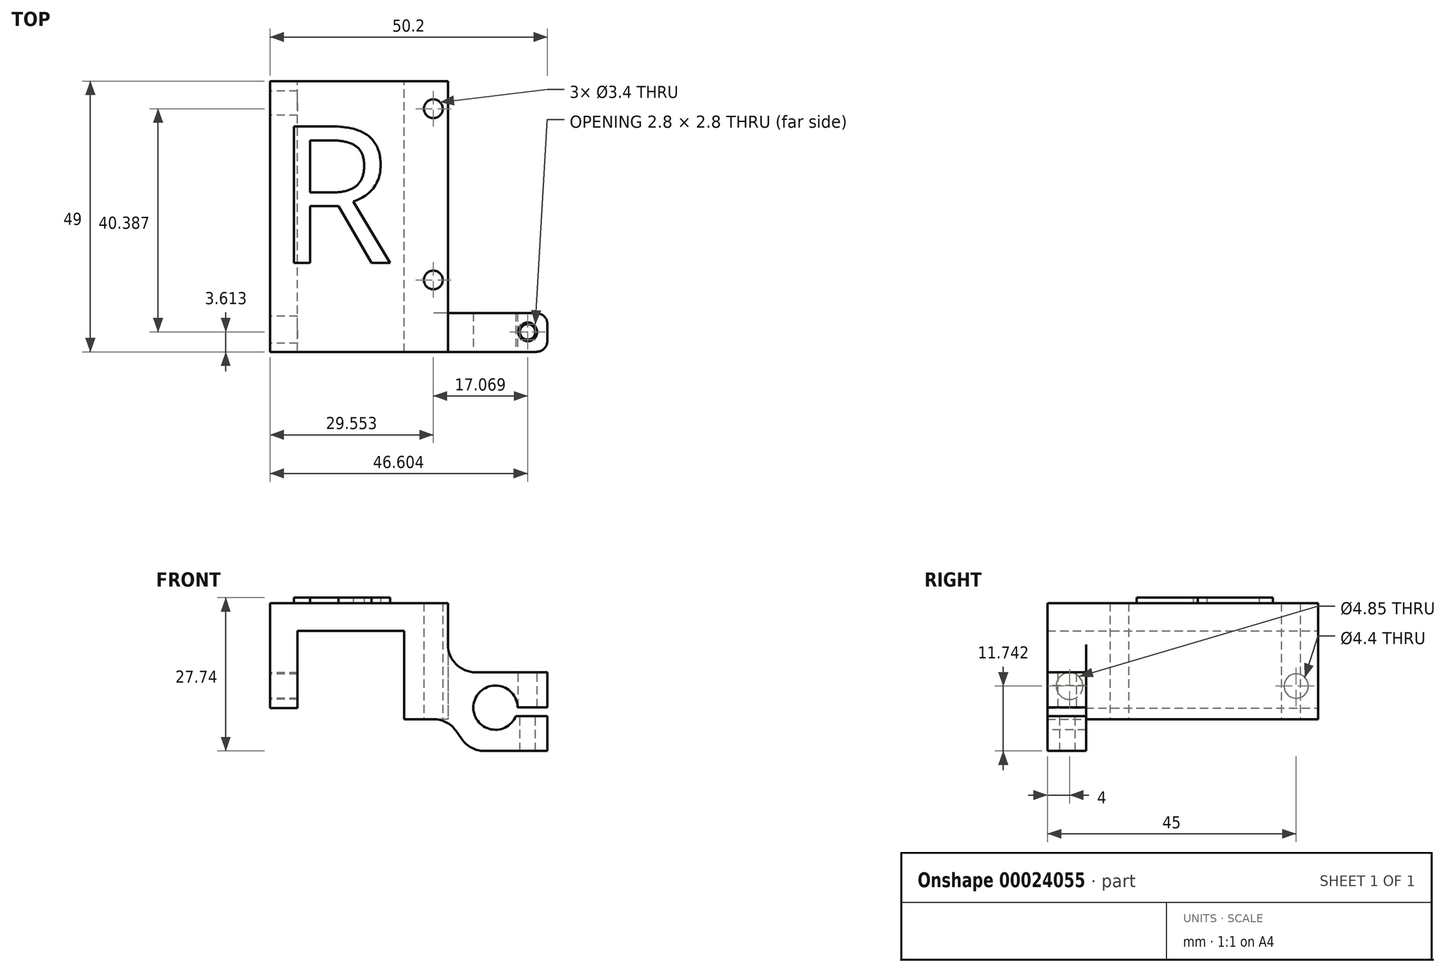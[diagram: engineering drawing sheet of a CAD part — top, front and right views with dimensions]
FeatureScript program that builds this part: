
annotation { "Feature Type Name" : "Feature", "Feature Type Description" : "" }
export const myFeature = defineFeature(function(context is Context, id is Id, definition is map)
    precondition{}
    {
        {
            var Q0;
            Q0=qCreatedBy(makeId("Front.planeOp"),FACE);
            var sketch = newSketch(context, id + "F0", { "sketchPlane" : qUnion([Q0])});
            skLineSegment(sketch, "E0", {"start": v(-18.67, 10.9) * mm, "end": v(-18.67, 29.9) * mm});
            skLineSegment(sketch, "E1", {"start": v(-18.67, 29.9) * mm, "end": v(13.53, 29.9) * mm});
            skLineSegment(sketch, "E2", {"start": v(13.53, 29.9) * mm, "end": v(13.53, 17.4) * mm});
            skLineSegment(sketch, "E3", {"start": v(5.63, 8.9) * mm, "end": v(5.63, 24.9) * mm});
            skLineSegment(sketch, "E4", {"start": v(5.63, 24.9) * mm, "end": v(-13.67, 24.9) * mm});
            skLineSegment(sketch, "E5", {"start": v(-13.67, 24.9) * mm, "end": v(-13.67, 10.9) * mm});
            skLineSegment(sketch, "E6", {"start": v(-13.67, 10.9) * mm, "end": v(-18.67, 10.9) * mm});
            skLineSegment(sketch, "E7", {"start": v(13.53, 17.4) * mm, "end": v(13.53, 8.9) * mm});
            skLineSegment(sketch, "E8", {"start": v(13.53, 8.9) * mm, "end": v(5.63, 8.9) * mm});
            skLineSegment(sketch, "E9", {"start": v(13.53, 17.4) * mm, "end": v(13.53, 17.4) * mm});
            skLineSegment(sketch, "E10", {"start": v(31.53, 17.36) * mm, "end": v(31.53, 11.06) * mm});
            skLineSegment(sketch, "E11", {"start": v(31.53, 11.06) * mm, "end": v(24.33, 11.06) * mm});
            skLineSegment(sketch, "E12", {"start": v(24.33, 11.06) * mm, "end": v(24.33, 9.45) * mm});
            skLineSegment(sketch, "E13", {"start": v(24.33, 9.45) * mm, "end": v(31.53, 9.45) * mm});
            skLineSegment(sketch, "E14", {"start": v(31.53, 9.45) * mm, "end": v(31.53, 3.15) * mm});
            skLineSegment(sketch, "E15", {"start": v(31.53, 3.15) * mm, "end": v(17.53, 3.15) * mm});
            skLineSegment(sketch, "E16", {"start": v(17.53, 3.15) * mm, "end": v(13.53, 8.9) * mm});
            skLineSegment(sketch, "E17", {"start": v(31.53, 17.36) * mm, "end": v(13.53, 17.4) * mm});
            skSolve(sketch);
        }
        {
            var Q0;
            Q0=makeQuery(id+"F0.imprint","IMPRINT",FACE,{"disambiguationData":[TD([[makeQuery(id+"F0.imprint","IMPRINT",EDGE,{"derivedFrom":sQuery(id+"F0.wireOp",EDGE,"E0")}),-1.0]])]});
            var Q1;
            {var subQ2=sQuery(id+"F0.wireOp",EDGE,"69cbcc5d-e0c3-48db-8baf-3487a8abab7d");Q1=makeQuery(id+"F0.imprint","IMPRINT",FACE,{"disambiguationData":[TD([[makeQuery(id+"F0.imprint","IMPRINT",EDGE,{"derivedFrom":subQ2}),-1.0]])]});}
            var Q2;
            Q2=makeQuery(id+"F0.imprint","IMPRINT",FACE,{"disambiguationData":[TD([[makeQuery(id+"F0.imprint","IMPRINT",EDGE,{"derivedFrom":sQuery(id+"F0.wireOp",EDGE,"E7")}),1.0]])]});
            extrude(context, id + "F1", {"entities" : qUnion([Q0, Q1, Q2]), "depth" : 7 * mm});
        }
        {
            var Q0;
            Q0=makeQuery(id+"F0.imprint","IMPRINT",FACE,{"disambiguationData":[TD([[makeQuery(id+"F0.imprint","IMPRINT",EDGE,{"derivedFrom":sQuery(id+"F0.wireOp",EDGE,"E0")}),-1.0]])]});
            extrude(context, id + "F2", {"entities" : qUnion([Q0]), "operationType" : NewBodyOperationType.ADD, "oppositeDirection" : true, "depth" : 42 * mm});
        }
        {
            var Q0;
            {var subQ0=sQuery(id+"F0.wireOp",EDGE,"E8");Q0=makeQuery(id+"F2.boolean.opBoolean","MERGE",FACE,{"derivedFrom":[makeQuery(id+"F1.opExtrude","SWEPT_FACE",FACE,{"disambiguationData":[OSD([subQ0])]}),makeQuery(id+"F2.opExtrude","SWEPT_FACE",FACE,{"disambiguationData":[OSD([subQ0])]})]});}
            var sketch = newSketch(context, id + "F3", { "sketchPlane" : qUnion([Q0])});
            skCircle(sketch, "E18", {"center": v(10.88, -6) * mm, "radius": 1.7 * mm});
            skCircle(sketch, "E19", {"center": v(10.88, -37) * mm, "radius": 1.7 * mm});
            skCircle(sketch, "E20", {"center": v(26.38, -21.5) * mm, "radius": 11 * mm});
            skSolve(sketch);
        }
        {
            var Q0;
            Q0=qSketchRegion(id+"F3",true);
            extrude(context, id + "F4", {"entities" : qUnion([Q0]), "operationType" : NewBodyOperationType.REMOVE, "endBound" : BoundingType.THROUGH_ALL, "oppositeDirection" : true, "depth" : 25 * mm});
        }
        {
            var Q0;
            Q0=makeQuery(id+"F1.opExtrude","CAP_FACE",FACE,{"disambiguationData":[OSD([sQuery(id+"F0.wireOp",EDGE,"E0"),sQuery(id+"F0.wireOp",EDGE,"E1"),sQuery(id+"F0.wireOp",EDGE,"E2"),sQuery(id+"F0.wireOp",EDGE,"E3"),sQuery(id+"F0.wireOp",EDGE,"E4"),sQuery(id+"F0.wireOp",EDGE,"E5"),sQuery(id+"F0.wireOp",EDGE,"E6"),sQuery(id+"F0.wireOp",EDGE,"E8"),sQuery(id+"F0.wireOp",EDGE,"E9"),sQuery(id+"F0.wireOp",EDGE,"58f11638-63e7-4b32-8aff-a1ba3c53649b"),sQuery(id+"F0.wireOp",EDGE,"E10"),sQuery(id+"F0.wireOp",EDGE,"E11"),sQuery(id+"F0.wireOp",EDGE,"E12"),sQuery(id+"F0.wireOp",EDGE,"E13"),sQuery(id+"F0.wireOp",EDGE,"E14"),sQuery(id+"F0.wireOp",EDGE,"E15"),sQuery(id+"F0.wireOp",EDGE,"E16")])],"isStart":false});
            var sketch = newSketch(context, id + "F5", { "sketchPlane" : qUnion([Q0])});
            skCircle(sketch, "E21", {"center": v(22.13, 10.98) * mm, "radius": 4 * mm});
            skSolve(sketch);
        }
        {
            var Q0;
            Q0=qSketchRegion(id+"F5",true);
            extrude(context, id + "F6", {"entities" : qUnion([Q0]), "operationType" : NewBodyOperationType.REMOVE, "oppositeDirection" : true, "depth" : 10 * mm});
        }
        {
            var Q0;
            Q0=qSketchRegion(id+"F3",true);
            extrude(context, id + "F7", {"entities" : qUnion([Q0]), "operationType" : NewBodyOperationType.REMOVE, "endBound" : BoundingType.THROUGH_ALL, "oppositeDirection" : true, "depth" : 25 * mm});
        }
        {
            var Q0;
            Q0=makeQuery(id+"F1.opExtrude","SWEPT_FACE",FACE,{"disambiguationData":[OSD([sQuery(id+"F0.wireOp",EDGE,"E17")])]});
            var sketch = newSketch(context, id + "F8", { "sketchPlane" : qUnion([Q0])});
            skCircle(sketch, "E22", {"center": v(27.93, -3.39) * mm, "radius": 1.7 * mm});
            skCircle(sketch, "E23", {"center": v(27.93, -3.39) * mm, "radius": 1.4 * mm});
            skSolve(sketch);
        }
        {
            var Q0;
            Q0=makeQuery(id+"F8.imprint","IMPRINT",FACE,{"disambiguationData":[TD([[makeQuery(id+"F8.imprint","IMPRINT",EDGE,{"derivedFrom":sQuery(id+"F8.wireOp",EDGE,"E23")}),1.0]])]});
            extrude(context, id + "F9", {"entities" : qUnion([Q0]), "operationType" : NewBodyOperationType.REMOVE, "endBound" : BoundingType.THROUGH_ALL, "oppositeDirection" : true, "depth" : 25 * mm});
        }
        {
            var Q0;
            Q0=makeQuery(id+"F8.imprint","IMPRINT",FACE,{"disambiguationData":[TD([[makeQuery(id+"F8.imprint","IMPRINT",EDGE,{"derivedFrom":sQuery(id+"F8.wireOp",EDGE,"E22")}),1.0]])]});
            extrude(context, id + "F10", {"entities" : qUnion([Q0]), "operationType" : NewBodyOperationType.REMOVE, "endBound" : BoundingType.UP_TO_NEXT, "oppositeDirection" : true, "depth" : 25 * mm});
        }
        {
            var Q0;
            Q0=makeQuery(id+"F1.opExtrude","SWEPT_EDGE",EDGE,{"disambiguationData":[OSD([sQuery(id+"F0.wireOp",EDGE,"E2"),sQuery(id+"F0.wireOp",EDGE,"E7"),sQuery(id+"F0.wireOp",EDGE,"E17")])]});
            fillet(context, id + "F11", {"entities" : qUnion([Q0]), "radius" : 5 * mm, "tangentPropagation" : true, "allowEdgeOverflow" : false});
        }
        {
            var Q0;
            Q0=makeQuery(id+"F1.opExtrude","SWEPT_EDGE",EDGE,{"disambiguationData":[OSD([sQuery(id+"F0.wireOp",EDGE,"E7"),sQuery(id+"F0.wireOp",EDGE,"E8"),sQuery(id+"F0.wireOp",EDGE,"E16")])]});
            fillet(context, id + "F12", {"entities" : qUnion([Q0]), "radius" : 5 * mm, "tangentPropagation" : true, "allowEdgeOverflow" : false});
        }
        {
            var Q0;
            Q0=makeQuery(id+"F1.opExtrude","SWEPT_EDGE",EDGE,{"disambiguationData":[OSD([sQuery(id+"F0.wireOp",EDGE,"E15"),sQuery(id+"F0.wireOp",EDGE,"E16")])]});
            fillet(context, id + "F13", {"entities" : qUnion([Q0]), "radius" : 5 * mm, "tangentPropagation" : true, "allowEdgeOverflow" : false});
        }
        {
            var Q0;
            Q0=makeQuery(id+"F1.opExtrude","CAP_EDGE",EDGE,{"disambiguationData":[OSD([sQuery(id+"F0.wireOp",EDGE,"E10")])],"isStart":false});
            var Q1;
            Q1=makeQuery(id+"F1.opExtrude","CAP_EDGE",EDGE,{"disambiguationData":[OSD([sQuery(id+"F0.wireOp",EDGE,"E14")])],"isStart":false});
            var Q2;
            Q2=makeQuery(id+"F1.opExtrude","CAP_EDGE",EDGE,{"disambiguationData":[OSD([sQuery(id+"F0.wireOp",EDGE,"E10")])],"isStart":true});
            var Q3;
            Q3=makeQuery(id+"F1.opExtrude","CAP_EDGE",EDGE,{"disambiguationData":[OSD([sQuery(id+"F0.wireOp",EDGE,"E14")])],"isStart":true});
            fillet(context, id + "F14", {"entities" : qUnion([Q0, Q1, Q2, Q3]), "radius" : 2 * mm, "tangentPropagation" : true, "allowEdgeOverflow" : false});
        }
        {
            var Q0;
            {var subQ0=sQuery(id+"F0.wireOp",EDGE,"E0");Q0=makeQuery(id+"F2.boolean.opBoolean","MERGE",FACE,{"derivedFrom":[makeQuery(id+"F1.opExtrude","SWEPT_FACE",FACE,{"disambiguationData":[OSD([subQ0])]}),makeQuery(id+"F2.opExtrude","SWEPT_FACE",FACE,{"disambiguationData":[OSD([subQ0])]})]});}
            var sketch = newSketch(context, id + "F15", { "sketchPlane" : qUnion([Q0])});
            skCircle(sketch, "E24", {"center": v(-38, 14.9) * mm, "radius": 2.2 * mm});
            skCircle(sketch, "E25", {"center": v(3, 14.9) * mm, "radius": 2.43 * mm});
            skSolve(sketch);
        }
        {
            var Q0;
            Q0=qSketchRegion(id+"F15",true);
            extrude(context, id + "F16", {"entities" : qUnion([Q0]), "operationType" : NewBodyOperationType.REMOVE, "oppositeDirection" : true, "depth" : 6 * mm});
        }
        {
            var Q0;
            {var subQ0=sQuery(id+"F0.wireOp",EDGE,"E1");Q0=makeQuery(id+"F2.boolean.opBoolean","MERGE",FACE,{"derivedFrom":[makeQuery(id+"F1.opExtrude","SWEPT_FACE",FACE,{"disambiguationData":[OSD([subQ0])]}),makeQuery(id+"F2.opExtrude","SWEPT_FACE",FACE,{"disambiguationData":[OSD([subQ0])]})]});}
            var sketch = newSketch(context, id + "F17", { "sketchPlane" : qUnion([Q0])});
            skText(sketch, "E26", { "text": "R", "fontName": "OpenSans-Regular.ttf"});
            const initialGuessF17  = {"E26": [-0.0177, 0.00911, 1, 0, 0.0249]};
            skSetInitialGuess(sketch, initialGuessF17);
            skSolve(sketch);
        }
        {
            var Q0;
            Q0=qSketchRegion(id+"F17",true);
            extrude(context, id + "F18", {"entities" : qUnion([Q0]), "operationType" : NewBodyOperationType.ADD, "depth" : 1 * mm});
        }
    });
